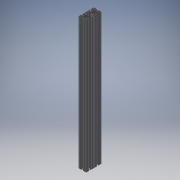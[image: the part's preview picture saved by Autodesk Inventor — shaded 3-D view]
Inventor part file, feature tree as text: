
AUTODESK INVENTOR PART (.ipt)
format: ipt  version: 2018 (Build 220112000, 112)  size: 633,856 bytes
history: native  units: mm
features: other x1, extrude x1, sketch x1
ambient origin geometry x8: Origin, YZ Plane, XZ Plane, XY Plane, X Axis, Y Axis, Z Axis, Center Point
bodies: Body1 (feature_tree)
feature tree (3):
  other  "Sólido1"
  extrude  "Extrusão1"  [1 undecoded]
  sketch  "Esboço1"  dims[d0=615.0mm d1=0.0mm]
note: 1 required parameter value undecoded (feature->parameter linkage not recoverable at this tier; creation-order binding heuristic only, values carry confidence <= 0.55)
